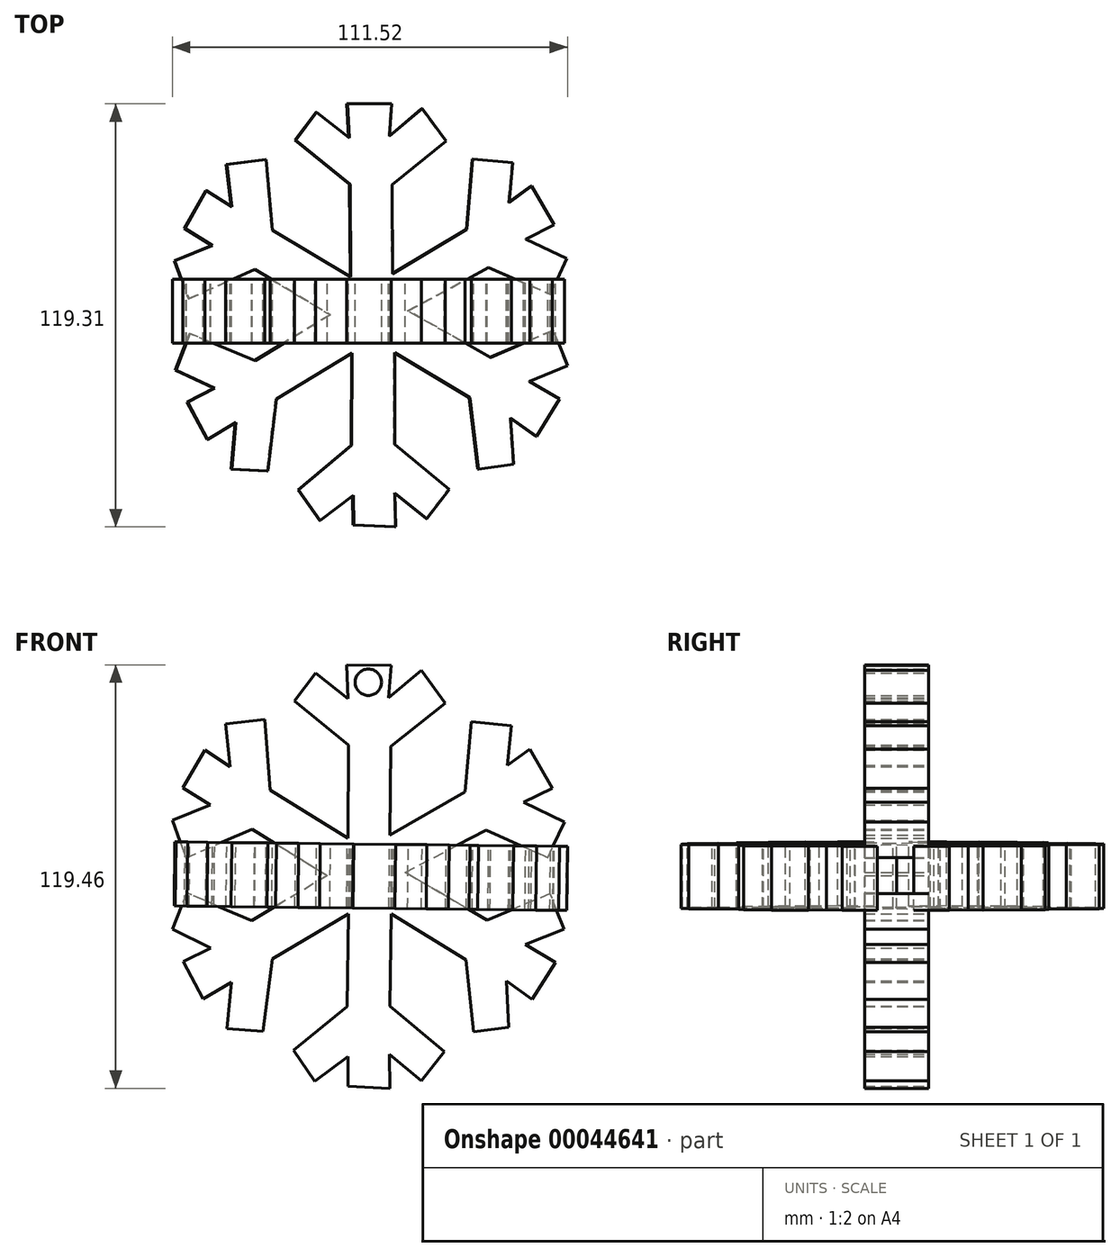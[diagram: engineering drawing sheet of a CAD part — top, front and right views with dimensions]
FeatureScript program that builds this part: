
annotation { "Feature Type Name" : "Feature", "Feature Type Description" : "" }
export const myFeature = defineFeature(function(context is Context, id is Id, definition is map)
    precondition{}
    {
        {
            var Q0;
            Q0=qCreatedBy(makeId("Front.planeOp"),FACE);
            var sketch = newSketch(context, id + "F0", { "sketchPlane" : qUnion([Q0])});
            skLineSegment(sketch, "E0", {"start": v(6.13, 11.69) * mm, "end": v(6.27, 36.78) * mm});
            skLineSegment(sketch, "E1", {"start": v(6.27, 36.78) * mm, "end": v(21.67, 48.9) * mm});
            skLineSegment(sketch, "E2", {"start": v(21.67, 48.9) * mm, "end": v(14.97, 58.16) * mm});
            skLineSegment(sketch, "E3", {"start": v(14.97, 58.16) * mm, "end": v(5.7, 50.46) * mm});
            skLineSegment(sketch, "E4", {"start": v(5.7, 50.46) * mm, "end": v(6.41, 59.58) * mm});
            skLineSegment(sketch, "E5", {"start": v(6.41, 59.58) * mm, "end": v(-6.13, 59.73) * mm});
            skLineSegment(sketch, "E6", {"start": v(-6.13, 59.73) * mm, "end": v(-5.7, 50.18) * mm});
            skLineSegment(sketch, "E7", {"start": v(-5.7, 50.18) * mm, "end": v(-14.82, 57.45) * mm});
            skLineSegment(sketch, "E8", {"start": v(-14.82, 57.45) * mm, "end": v(-20.81, 49.6) * mm});
            skLineSegment(sketch, "E9", {"start": v(-20.81, 49.6) * mm, "end": v(-5.56, 37.06) * mm});
            skLineSegment(sketch, "E10", {"start": v(-5.56, 37.06) * mm, "end": v(-5.7, 10.83) * mm});
            skLineSegment(sketch, "E11", {"start": v(-5.7, 10.83) * mm, "end": v(-27.65, 24.37) * mm});
            skLineSegment(sketch, "E12", {"start": v(-27.65, 24.37) * mm, "end": v(-29.22, 44.33) * mm});
            skLineSegment(sketch, "E13", {"start": v(-29.22, 44.33) * mm, "end": v(-40.34, 43.05) * mm});
            skLineSegment(sketch, "E14", {"start": v(-40.34, 43.05) * mm, "end": v(-39.06, 31.07) * mm});
            skLineSegment(sketch, "E15", {"start": v(-39.06, 31.07) * mm, "end": v(-46.18, 35.78) * mm});
            skLineSegment(sketch, "E16", {"start": v(-46.18, 35.78) * mm, "end": v(-52.31, 25.09) * mm});
            skLineSegment(sketch, "E17", {"start": v(-52.31, 25.09) * mm, "end": v(-44.62, 20.24) * mm});
            skLineSegment(sketch, "E18", {"start": v(-44.62, 20.24) * mm, "end": v(-55.3, 15.96) * mm});
            skLineSegment(sketch, "E19", {"start": v(-55.3, 15.96) * mm, "end": v(-51.46, 5.27) * mm});
            skLineSegment(sketch, "E20", {"start": v(-51.46, 5.27) * mm, "end": v(-32.79, 13.4) * mm});
            skLineSegment(sketch, "E21", {"start": v(-32.79, 13.4) * mm, "end": v(-11.55, 0.29) * mm});
            skLineSegment(sketch, "E22", {"start": v(-11.55, 0.29) * mm, "end": v(-32.93, -12.4) * mm});
            skLineSegment(sketch, "E23", {"start": v(-32.93, -12.4) * mm, "end": v(-51.32, -4.56) * mm});
            skLineSegment(sketch, "E24", {"start": v(-51.32, -4.56) * mm, "end": v(-55.3, -14.82) * mm});
            skLineSegment(sketch, "E25", {"start": v(-55.3, -14.82) * mm, "end": v(-44.47, -20.1) * mm});
            skLineSegment(sketch, "E26", {"start": v(-44.47, -20.1) * mm, "end": v(-52.17, -23.95) * mm});
            skLineSegment(sketch, "E27", {"start": v(-52.17, -23.95) * mm, "end": v(-46.61, -34.5) * mm});
            skLineSegment(sketch, "E28", {"start": v(-46.61, -34.5) * mm, "end": v(-38.63, -29.8) * mm});
            skLineSegment(sketch, "E29", {"start": v(-38.63, -29.8) * mm, "end": v(-39.91, -42.9) * mm});
            skLineSegment(sketch, "E30", {"start": v(-39.91, -42.9) * mm, "end": v(-29.8, -43.62) * mm});
            skLineSegment(sketch, "E31", {"start": v(-29.8, -43.62) * mm, "end": v(-27.08, -23.23) * mm});
            skLineSegment(sketch, "E32", {"start": v(-27.08, -23.23) * mm, "end": v(-5.56, -10.55) * mm});
            skLineSegment(sketch, "E33", {"start": v(-5.56, -10.55) * mm, "end": v(-5.99, -36.63) * mm});
            skLineSegment(sketch, "E34", {"start": v(-5.99, -36.63) * mm, "end": v(-21.1, -49.04) * mm});
            skLineSegment(sketch, "E35", {"start": v(-21.1, -49.04) * mm, "end": v(-15.1, -57.73) * mm});
            skLineSegment(sketch, "E36", {"start": v(-15.1, -57.73) * mm, "end": v(-5.7, -50.75) * mm});
            skLineSegment(sketch, "E37", {"start": v(-5.7, -50.75) * mm, "end": v(-5.7, -59.16) * mm});
            skLineSegment(sketch, "E38", {"start": v(-5.7, -59.16) * mm, "end": v(6.13, -59.73) * mm});
            skLineSegment(sketch, "E39", {"start": v(6.13, -59.73) * mm, "end": v(5.99, -50.18) * mm});
            skLineSegment(sketch, "E40", {"start": v(5.99, -50.18) * mm, "end": v(14.97, -57.59) * mm});
            skLineSegment(sketch, "E41", {"start": v(14.97, -57.59) * mm, "end": v(21.38, -49.32) * mm});
            skLineSegment(sketch, "E42", {"start": v(21.38, -49.32) * mm, "end": v(6.13, -36.5) * mm});
            skLineSegment(sketch, "E43", {"start": v(6.13, -36.5) * mm, "end": v(6.41, -10.55) * mm});
            skLineSegment(sketch, "E44", {"start": v(6.41, -10.55) * mm, "end": v(27.51, -23.52) * mm});
            skLineSegment(sketch, "E45", {"start": v(27.51, -23.52) * mm, "end": v(29.65, -43.76) * mm});
            skLineSegment(sketch, "E46", {"start": v(29.65, -43.76) * mm, "end": v(39.63, -42.48) * mm});
            skLineSegment(sketch, "E47", {"start": v(39.63, -42.48) * mm, "end": v(38.91, -29.36) * mm});
            skLineSegment(sketch, "E48", {"start": v(38.91, -29.36) * mm, "end": v(46.18, -34.64) * mm});
            skLineSegment(sketch, "E49", {"start": v(46.18, -34.64) * mm, "end": v(52.74, -24.23) * mm});
            skLineSegment(sketch, "E50", {"start": v(52.74, -24.23) * mm, "end": v(44.33, -19.1) * mm});
            skLineSegment(sketch, "E51", {"start": v(44.33, -19.1) * mm, "end": v(55.16, -14.82) * mm});
            skLineSegment(sketch, "E52", {"start": v(55.16, -14.82) * mm, "end": v(51.32, -4.85) * mm});
            skLineSegment(sketch, "E53", {"start": v(51.32, -4.85) * mm, "end": v(33.5, -12.26) * mm});
            skLineSegment(sketch, "E54", {"start": v(33.5, -12.26) * mm, "end": v(10.4, 1.14) * mm});
            skLineSegment(sketch, "E55", {"start": v(10.4, 1.14) * mm, "end": v(33.21, 13.11) * mm});
            skLineSegment(sketch, "E56", {"start": v(33.21, 13.11) * mm, "end": v(50.6, 5.42) * mm});
            skLineSegment(sketch, "E57", {"start": v(50.6, 5.42) * mm, "end": v(55.3, 15.4) * mm});
            skLineSegment(sketch, "E58", {"start": v(55.3, 15.4) * mm, "end": v(43.76, 20.95) * mm});
            skLineSegment(sketch, "E59", {"start": v(43.76, 20.95) * mm, "end": v(51.89, 24.95) * mm});
            skLineSegment(sketch, "E60", {"start": v(51.89, 24.95) * mm, "end": v(45.61, 35.92) * mm});
            skLineSegment(sketch, "E61", {"start": v(45.61, 35.92) * mm, "end": v(39.2, 31.36) * mm});
            skLineSegment(sketch, "E62", {"start": v(39.2, 31.36) * mm, "end": v(40.34, 42.62) * mm});
            skLineSegment(sketch, "E63", {"start": v(40.34, 42.62) * mm, "end": v(29.08, 43.76) * mm});
            skLineSegment(sketch, "E64", {"start": v(29.08, 43.76) * mm, "end": v(27.23, 23.95) * mm});
            skLineSegment(sketch, "E65", {"start": v(27.23, 23.95) * mm, "end": v(6.13, 11.69) * mm});
            skSolve(sketch);
        }
        {
            var Q0;
            Q0 = qSketchRegion(id + "F0", true);
            extrude(context, id + "F1", {"entities" : qUnion([Q0]), "depth" : 18.08 * mm});
        }
        {
            var Q0;
            Q0=makeQuery(id+"F1.opExtrude","SWEPT_BODY",BODY,{"disambiguationData":[OSD([sQuery(id+"F0.wireOp",EDGE,"E0"),sQuery(id+"F0.wireOp",EDGE,"E1"),sQuery(id+"F0.wireOp",EDGE,"E2"),sQuery(id+"F0.wireOp",EDGE,"E3"),sQuery(id+"F0.wireOp",EDGE,"E4"),sQuery(id+"F0.wireOp",EDGE,"E5"),sQuery(id+"F0.wireOp",EDGE,"E6"),sQuery(id+"F0.wireOp",EDGE,"E7"),sQuery(id+"F0.wireOp",EDGE,"E8"),sQuery(id+"F0.wireOp",EDGE,"E9"),sQuery(id+"F0.wireOp",EDGE,"E10"),sQuery(id+"F0.wireOp",EDGE,"E11"),sQuery(id+"F0.wireOp",EDGE,"E12"),sQuery(id+"F0.wireOp",EDGE,"E13"),sQuery(id+"F0.wireOp",EDGE,"E14"),sQuery(id+"F0.wireOp",EDGE,"E15"),sQuery(id+"F0.wireOp",EDGE,"E16"),sQuery(id+"F0.wireOp",EDGE,"E17"),sQuery(id+"F0.wireOp",EDGE,"E18"),sQuery(id+"F0.wireOp",EDGE,"E19"),sQuery(id+"F0.wireOp",EDGE,"E20"),sQuery(id+"F0.wireOp",EDGE,"E21"),sQuery(id+"F0.wireOp",EDGE,"E22"),sQuery(id+"F0.wireOp",EDGE,"E23"),sQuery(id+"F0.wireOp",EDGE,"E24"),sQuery(id+"F0.wireOp",EDGE,"E25"),sQuery(id+"F0.wireOp",EDGE,"E26"),sQuery(id+"F0.wireOp",EDGE,"E27"),sQuery(id+"F0.wireOp",EDGE,"E28"),sQuery(id+"F0.wireOp",EDGE,"E29"),sQuery(id+"F0.wireOp",EDGE,"E30"),sQuery(id+"F0.wireOp",EDGE,"E31"),sQuery(id+"F0.wireOp",EDGE,"E32"),sQuery(id+"F0.wireOp",EDGE,"E33"),sQuery(id+"F0.wireOp",EDGE,"E34"),sQuery(id+"F0.wireOp",EDGE,"E35"),sQuery(id+"F0.wireOp",EDGE,"E36"),sQuery(id+"F0.wireOp",EDGE,"E37"),sQuery(id+"F0.wireOp",EDGE,"E38"),sQuery(id+"F0.wireOp",EDGE,"E39"),sQuery(id+"F0.wireOp",EDGE,"E40"),sQuery(id+"F0.wireOp",EDGE,"E41"),sQuery(id+"F0.wireOp",EDGE,"E42"),sQuery(id+"F0.wireOp",EDGE,"E43"),sQuery(id+"F0.wireOp",EDGE,"E44"),sQuery(id+"F0.wireOp",EDGE,"E45"),sQuery(id+"F0.wireOp",EDGE,"E46"),sQuery(id+"F0.wireOp",EDGE,"E47"),sQuery(id+"F0.wireOp",EDGE,"E48"),sQuery(id+"F0.wireOp",EDGE,"E49"),sQuery(id+"F0.wireOp",EDGE,"E50"),sQuery(id+"F0.wireOp",EDGE,"E51"),sQuery(id+"F0.wireOp",EDGE,"E52"),sQuery(id+"F0.wireOp",EDGE,"E53"),sQuery(id+"F0.wireOp",EDGE,"E54"),sQuery(id+"F0.wireOp",EDGE,"E55"),sQuery(id+"F0.wireOp",EDGE,"E56"),sQuery(id+"F0.wireOp",EDGE,"E57"),sQuery(id+"F0.wireOp",EDGE,"E58"),sQuery(id+"F0.wireOp",EDGE,"E59"),sQuery(id+"F0.wireOp",EDGE,"E60"),sQuery(id+"F0.wireOp",EDGE,"E61"),sQuery(id+"F0.wireOp",EDGE,"E62"),sQuery(id+"F0.wireOp",EDGE,"E63"),sQuery(id+"F0.wireOp",EDGE,"E64"),sQuery(id+"F0.wireOp",EDGE,"E65")])]});
            var Q1;
            Q1=makeQuery(id+"F1.opExtrude","CAP_FACE",FACE,{"disambiguationData":[OSD([sQuery(id+"F0.wireOp",EDGE,"E0"),sQuery(id+"F0.wireOp",EDGE,"E1"),sQuery(id+"F0.wireOp",EDGE,"E2"),sQuery(id+"F0.wireOp",EDGE,"E3"),sQuery(id+"F0.wireOp",EDGE,"E4"),sQuery(id+"F0.wireOp",EDGE,"E5"),sQuery(id+"F0.wireOp",EDGE,"E6"),sQuery(id+"F0.wireOp",EDGE,"E7"),sQuery(id+"F0.wireOp",EDGE,"E8"),sQuery(id+"F0.wireOp",EDGE,"E9"),sQuery(id+"F0.wireOp",EDGE,"E10"),sQuery(id+"F0.wireOp",EDGE,"E11"),sQuery(id+"F0.wireOp",EDGE,"E12"),sQuery(id+"F0.wireOp",EDGE,"E13"),sQuery(id+"F0.wireOp",EDGE,"E14"),sQuery(id+"F0.wireOp",EDGE,"E15"),sQuery(id+"F0.wireOp",EDGE,"E16"),sQuery(id+"F0.wireOp",EDGE,"E17"),sQuery(id+"F0.wireOp",EDGE,"E18"),sQuery(id+"F0.wireOp",EDGE,"E19"),sQuery(id+"F0.wireOp",EDGE,"E20"),sQuery(id+"F0.wireOp",EDGE,"E21"),sQuery(id+"F0.wireOp",EDGE,"E22"),sQuery(id+"F0.wireOp",EDGE,"E23"),sQuery(id+"F0.wireOp",EDGE,"E24"),sQuery(id+"F0.wireOp",EDGE,"E25"),sQuery(id+"F0.wireOp",EDGE,"E26"),sQuery(id+"F0.wireOp",EDGE,"E27"),sQuery(id+"F0.wireOp",EDGE,"E28"),sQuery(id+"F0.wireOp",EDGE,"E29"),sQuery(id+"F0.wireOp",EDGE,"E30"),sQuery(id+"F0.wireOp",EDGE,"E31"),sQuery(id+"F0.wireOp",EDGE,"E32"),sQuery(id+"F0.wireOp",EDGE,"E33"),sQuery(id+"F0.wireOp",EDGE,"E34"),sQuery(id+"F0.wireOp",EDGE,"E35"),sQuery(id+"F0.wireOp",EDGE,"E36"),sQuery(id+"F0.wireOp",EDGE,"E37"),sQuery(id+"F0.wireOp",EDGE,"E38"),sQuery(id+"F0.wireOp",EDGE,"E39"),sQuery(id+"F0.wireOp",EDGE,"E40"),sQuery(id+"F0.wireOp",EDGE,"E41"),sQuery(id+"F0.wireOp",EDGE,"E42"),sQuery(id+"F0.wireOp",EDGE,"E43"),sQuery(id+"F0.wireOp",EDGE,"E44"),sQuery(id+"F0.wireOp",EDGE,"E45"),sQuery(id+"F0.wireOp",EDGE,"E46"),sQuery(id+"F0.wireOp",EDGE,"E47"),sQuery(id+"F0.wireOp",EDGE,"E48"),sQuery(id+"F0.wireOp",EDGE,"E49"),sQuery(id+"F0.wireOp",EDGE,"E50"),sQuery(id+"F0.wireOp",EDGE,"E51"),sQuery(id+"F0.wireOp",EDGE,"E52"),sQuery(id+"F0.wireOp",EDGE,"E53"),sQuery(id+"F0.wireOp",EDGE,"E54"),sQuery(id+"F0.wireOp",EDGE,"E55"),sQuery(id+"F0.wireOp",EDGE,"E56"),sQuery(id+"F0.wireOp",EDGE,"E57"),sQuery(id+"F0.wireOp",EDGE,"E58"),sQuery(id+"F0.wireOp",EDGE,"E59"),sQuery(id+"F0.wireOp",EDGE,"E60"),sQuery(id+"F0.wireOp",EDGE,"E61"),sQuery(id+"F0.wireOp",EDGE,"E62"),sQuery(id+"F0.wireOp",EDGE,"E63"),sQuery(id+"F0.wireOp",EDGE,"E64"),sQuery(id+"F0.wireOp",EDGE,"E65")])],"isStart":false});
            mirror(context, id + "F2", {"entities" : qUnion([Q0]), "mirrorPlane" : qUnion([Q1])});
        }
        {
            var Q0;
            Q0=makeQuery(id+"F2.opPattern","COPY",BODY,{"derivedFrom":makeQuery(id+"F1.opExtrude","SWEPT_BODY",BODY,{"disambiguationData":[OSD([sQuery(id+"F0.wireOp",EDGE,"E0"),sQuery(id+"F0.wireOp",EDGE,"E1"),sQuery(id+"F0.wireOp",EDGE,"E2"),sQuery(id+"F0.wireOp",EDGE,"E3"),sQuery(id+"F0.wireOp",EDGE,"E4"),sQuery(id+"F0.wireOp",EDGE,"E5"),sQuery(id+"F0.wireOp",EDGE,"E6"),sQuery(id+"F0.wireOp",EDGE,"E7"),sQuery(id+"F0.wireOp",EDGE,"E8"),sQuery(id+"F0.wireOp",EDGE,"E9"),sQuery(id+"F0.wireOp",EDGE,"E10"),sQuery(id+"F0.wireOp",EDGE,"E11"),sQuery(id+"F0.wireOp",EDGE,"E12"),sQuery(id+"F0.wireOp",EDGE,"E13"),sQuery(id+"F0.wireOp",EDGE,"E14"),sQuery(id+"F0.wireOp",EDGE,"E15"),sQuery(id+"F0.wireOp",EDGE,"E16"),sQuery(id+"F0.wireOp",EDGE,"E17"),sQuery(id+"F0.wireOp",EDGE,"E18"),sQuery(id+"F0.wireOp",EDGE,"E19"),sQuery(id+"F0.wireOp",EDGE,"E20"),sQuery(id+"F0.wireOp",EDGE,"E21"),sQuery(id+"F0.wireOp",EDGE,"E22"),sQuery(id+"F0.wireOp",EDGE,"E23"),sQuery(id+"F0.wireOp",EDGE,"E24"),sQuery(id+"F0.wireOp",EDGE,"E25"),sQuery(id+"F0.wireOp",EDGE,"E26"),sQuery(id+"F0.wireOp",EDGE,"E27"),sQuery(id+"F0.wireOp",EDGE,"E28"),sQuery(id+"F0.wireOp",EDGE,"E29"),sQuery(id+"F0.wireOp",EDGE,"E30"),sQuery(id+"F0.wireOp",EDGE,"E31"),sQuery(id+"F0.wireOp",EDGE,"E32"),sQuery(id+"F0.wireOp",EDGE,"E33"),sQuery(id+"F0.wireOp",EDGE,"E34"),sQuery(id+"F0.wireOp",EDGE,"E35"),sQuery(id+"F0.wireOp",EDGE,"E36"),sQuery(id+"F0.wireOp",EDGE,"E37"),sQuery(id+"F0.wireOp",EDGE,"E38"),sQuery(id+"F0.wireOp",EDGE,"E39"),sQuery(id+"F0.wireOp",EDGE,"E40"),sQuery(id+"F0.wireOp",EDGE,"E41"),sQuery(id+"F0.wireOp",EDGE,"E42"),sQuery(id+"F0.wireOp",EDGE,"E43"),sQuery(id+"F0.wireOp",EDGE,"E44"),sQuery(id+"F0.wireOp",EDGE,"E45"),sQuery(id+"F0.wireOp",EDGE,"E46"),sQuery(id+"F0.wireOp",EDGE,"E47"),sQuery(id+"F0.wireOp",EDGE,"E48"),sQuery(id+"F0.wireOp",EDGE,"E49"),sQuery(id+"F0.wireOp",EDGE,"E50"),sQuery(id+"F0.wireOp",EDGE,"E51"),sQuery(id+"F0.wireOp",EDGE,"E52"),sQuery(id+"F0.wireOp",EDGE,"E53"),sQuery(id+"F0.wireOp",EDGE,"E54"),sQuery(id+"F0.wireOp",EDGE,"E55"),sQuery(id+"F0.wireOp",EDGE,"E56"),sQuery(id+"F0.wireOp",EDGE,"E57"),sQuery(id+"F0.wireOp",EDGE,"E58"),sQuery(id+"F0.wireOp",EDGE,"E59"),sQuery(id+"F0.wireOp",EDGE,"E60"),sQuery(id+"F0.wireOp",EDGE,"E61"),sQuery(id+"F0.wireOp",EDGE,"E62"),sQuery(id+"F0.wireOp",EDGE,"E63"),sQuery(id+"F0.wireOp",EDGE,"E64"),sQuery(id+"F0.wireOp",EDGE,"E65")])]}),"instanceName":"1"});
            transform(context, id + "F3", {"entities" : qUnion([Q0]), "transformType" : TransformType.TRANSLATION_3D, "dx" : 0 * mm, "dy" : 16.93 * mm, "dz" : 130.11 * mm, "makeCopy" : false});
        }
        {
            var Q0;
            Q0=makeQuery(id+"F2.opPattern","COPY",BODY,{"derivedFrom":makeQuery(id+"F1.opExtrude","SWEPT_BODY",BODY,{"disambiguationData":[OSD([sQuery(id+"F0.wireOp",EDGE,"E0"),sQuery(id+"F0.wireOp",EDGE,"E1"),sQuery(id+"F0.wireOp",EDGE,"E2"),sQuery(id+"F0.wireOp",EDGE,"E3"),sQuery(id+"F0.wireOp",EDGE,"E4"),sQuery(id+"F0.wireOp",EDGE,"E5"),sQuery(id+"F0.wireOp",EDGE,"E6"),sQuery(id+"F0.wireOp",EDGE,"E7"),sQuery(id+"F0.wireOp",EDGE,"E8"),sQuery(id+"F0.wireOp",EDGE,"E9"),sQuery(id+"F0.wireOp",EDGE,"E10"),sQuery(id+"F0.wireOp",EDGE,"E11"),sQuery(id+"F0.wireOp",EDGE,"E12"),sQuery(id+"F0.wireOp",EDGE,"E13"),sQuery(id+"F0.wireOp",EDGE,"E14"),sQuery(id+"F0.wireOp",EDGE,"E15"),sQuery(id+"F0.wireOp",EDGE,"E16"),sQuery(id+"F0.wireOp",EDGE,"E17"),sQuery(id+"F0.wireOp",EDGE,"E18"),sQuery(id+"F0.wireOp",EDGE,"E19"),sQuery(id+"F0.wireOp",EDGE,"E20"),sQuery(id+"F0.wireOp",EDGE,"E21"),sQuery(id+"F0.wireOp",EDGE,"E22"),sQuery(id+"F0.wireOp",EDGE,"E23"),sQuery(id+"F0.wireOp",EDGE,"E24"),sQuery(id+"F0.wireOp",EDGE,"E25"),sQuery(id+"F0.wireOp",EDGE,"E26"),sQuery(id+"F0.wireOp",EDGE,"E27"),sQuery(id+"F0.wireOp",EDGE,"E28"),sQuery(id+"F0.wireOp",EDGE,"E29"),sQuery(id+"F0.wireOp",EDGE,"E30"),sQuery(id+"F0.wireOp",EDGE,"E31"),sQuery(id+"F0.wireOp",EDGE,"E32"),sQuery(id+"F0.wireOp",EDGE,"E33"),sQuery(id+"F0.wireOp",EDGE,"E34"),sQuery(id+"F0.wireOp",EDGE,"E35"),sQuery(id+"F0.wireOp",EDGE,"E36"),sQuery(id+"F0.wireOp",EDGE,"E37"),sQuery(id+"F0.wireOp",EDGE,"E38"),sQuery(id+"F0.wireOp",EDGE,"E39"),sQuery(id+"F0.wireOp",EDGE,"E40"),sQuery(id+"F0.wireOp",EDGE,"E41"),sQuery(id+"F0.wireOp",EDGE,"E42"),sQuery(id+"F0.wireOp",EDGE,"E43"),sQuery(id+"F0.wireOp",EDGE,"E44"),sQuery(id+"F0.wireOp",EDGE,"E45"),sQuery(id+"F0.wireOp",EDGE,"E46"),sQuery(id+"F0.wireOp",EDGE,"E47"),sQuery(id+"F0.wireOp",EDGE,"E48"),sQuery(id+"F0.wireOp",EDGE,"E49"),sQuery(id+"F0.wireOp",EDGE,"E50"),sQuery(id+"F0.wireOp",EDGE,"E51"),sQuery(id+"F0.wireOp",EDGE,"E52"),sQuery(id+"F0.wireOp",EDGE,"E53"),sQuery(id+"F0.wireOp",EDGE,"E54"),sQuery(id+"F0.wireOp",EDGE,"E55"),sQuery(id+"F0.wireOp",EDGE,"E56"),sQuery(id+"F0.wireOp",EDGE,"E57"),sQuery(id+"F0.wireOp",EDGE,"E58"),sQuery(id+"F0.wireOp",EDGE,"E59"),sQuery(id+"F0.wireOp",EDGE,"E60"),sQuery(id+"F0.wireOp",EDGE,"E61"),sQuery(id+"F0.wireOp",EDGE,"E62"),sQuery(id+"F0.wireOp",EDGE,"E63"),sQuery(id+"F0.wireOp",EDGE,"E64"),sQuery(id+"F0.wireOp",EDGE,"E65")])]}),"instanceName":"1"});
            var Q1;
            Q1=makeQuery(id+"F2.opPattern","COPY",EDGE,{"derivedFrom":makeQuery(id+"F1.opExtrude","CAP_EDGE",EDGE,{"disambiguationData":[OSD([sQuery(id+"F0.wireOp",EDGE,"E5")])],"isStart":false}),"instanceName":"1"});
            transform(context, id + "F4", {"entities" : qUnion([Q0]), "transformType" : TransformType.ROTATION, "transformAxis" : qUnion([Q1]), "angle" : 90 * degree, "makeCopy" : false});
        }
        {
            var Q0;
            Q0=makeQuery(id+"F2.opPattern","COPY",BODY,{"derivedFrom":makeQuery(id+"F1.opExtrude","SWEPT_BODY",BODY,{"disambiguationData":[OSD([sQuery(id+"F0.wireOp",EDGE,"E0"),sQuery(id+"F0.wireOp",EDGE,"E1"),sQuery(id+"F0.wireOp",EDGE,"E2"),sQuery(id+"F0.wireOp",EDGE,"E3"),sQuery(id+"F0.wireOp",EDGE,"E4"),sQuery(id+"F0.wireOp",EDGE,"E5"),sQuery(id+"F0.wireOp",EDGE,"E6"),sQuery(id+"F0.wireOp",EDGE,"E7"),sQuery(id+"F0.wireOp",EDGE,"E8"),sQuery(id+"F0.wireOp",EDGE,"E9"),sQuery(id+"F0.wireOp",EDGE,"E10"),sQuery(id+"F0.wireOp",EDGE,"E11"),sQuery(id+"F0.wireOp",EDGE,"E12"),sQuery(id+"F0.wireOp",EDGE,"E13"),sQuery(id+"F0.wireOp",EDGE,"E14"),sQuery(id+"F0.wireOp",EDGE,"E15"),sQuery(id+"F0.wireOp",EDGE,"E16"),sQuery(id+"F0.wireOp",EDGE,"E17"),sQuery(id+"F0.wireOp",EDGE,"E18"),sQuery(id+"F0.wireOp",EDGE,"E19"),sQuery(id+"F0.wireOp",EDGE,"E20"),sQuery(id+"F0.wireOp",EDGE,"E21"),sQuery(id+"F0.wireOp",EDGE,"E22"),sQuery(id+"F0.wireOp",EDGE,"E23"),sQuery(id+"F0.wireOp",EDGE,"E24"),sQuery(id+"F0.wireOp",EDGE,"E25"),sQuery(id+"F0.wireOp",EDGE,"E26"),sQuery(id+"F0.wireOp",EDGE,"E27"),sQuery(id+"F0.wireOp",EDGE,"E28"),sQuery(id+"F0.wireOp",EDGE,"E29"),sQuery(id+"F0.wireOp",EDGE,"E30"),sQuery(id+"F0.wireOp",EDGE,"E31"),sQuery(id+"F0.wireOp",EDGE,"E32"),sQuery(id+"F0.wireOp",EDGE,"E33"),sQuery(id+"F0.wireOp",EDGE,"E34"),sQuery(id+"F0.wireOp",EDGE,"E35"),sQuery(id+"F0.wireOp",EDGE,"E36"),sQuery(id+"F0.wireOp",EDGE,"E37"),sQuery(id+"F0.wireOp",EDGE,"E38"),sQuery(id+"F0.wireOp",EDGE,"E39"),sQuery(id+"F0.wireOp",EDGE,"E40"),sQuery(id+"F0.wireOp",EDGE,"E41"),sQuery(id+"F0.wireOp",EDGE,"E42"),sQuery(id+"F0.wireOp",EDGE,"E43"),sQuery(id+"F0.wireOp",EDGE,"E44"),sQuery(id+"F0.wireOp",EDGE,"E45"),sQuery(id+"F0.wireOp",EDGE,"E46"),sQuery(id+"F0.wireOp",EDGE,"E47"),sQuery(id+"F0.wireOp",EDGE,"E48"),sQuery(id+"F0.wireOp",EDGE,"E49"),sQuery(id+"F0.wireOp",EDGE,"E50"),sQuery(id+"F0.wireOp",EDGE,"E51"),sQuery(id+"F0.wireOp",EDGE,"E52"),sQuery(id+"F0.wireOp",EDGE,"E53"),sQuery(id+"F0.wireOp",EDGE,"E54"),sQuery(id+"F0.wireOp",EDGE,"E55"),sQuery(id+"F0.wireOp",EDGE,"E56"),sQuery(id+"F0.wireOp",EDGE,"E57"),sQuery(id+"F0.wireOp",EDGE,"E58"),sQuery(id+"F0.wireOp",EDGE,"E59"),sQuery(id+"F0.wireOp",EDGE,"E60"),sQuery(id+"F0.wireOp",EDGE,"E61"),sQuery(id+"F0.wireOp",EDGE,"E62"),sQuery(id+"F0.wireOp",EDGE,"E63"),sQuery(id+"F0.wireOp",EDGE,"E64"),sQuery(id+"F0.wireOp",EDGE,"E65")])]}),"instanceName":"1"});
            transform(context, id + "F5", {"entities" : qUnion([Q0]), "transformType" : TransformType.TRANSLATION_3D, "dx" : 0 * mm, "dy" : 50.58 * mm, "dz" : -198.66 * mm, "makeCopy" : false});
        }
        {
            var Q0;
            Q0=qCreatedBy(makeId("Front.planeOp"),FACE);
            var sketch = newSketch(context, id + "F6", { "sketchPlane" : qUnion([Q0])});
            skCircle(sketch, "E66", {"center": v(0, 54.84) * mm, "radius": 3.72 * mm});
            skSolve(sketch);
        }
        {
            var Q0;
            Q0 = qSketchRegion(id + "F6", true);
            extrude(context, id + "F7", {"entities" : qUnion([Q0]), "operationType" : NewBodyOperationType.REMOVE, "depth" : 43.87 * mm});
        }
    });
